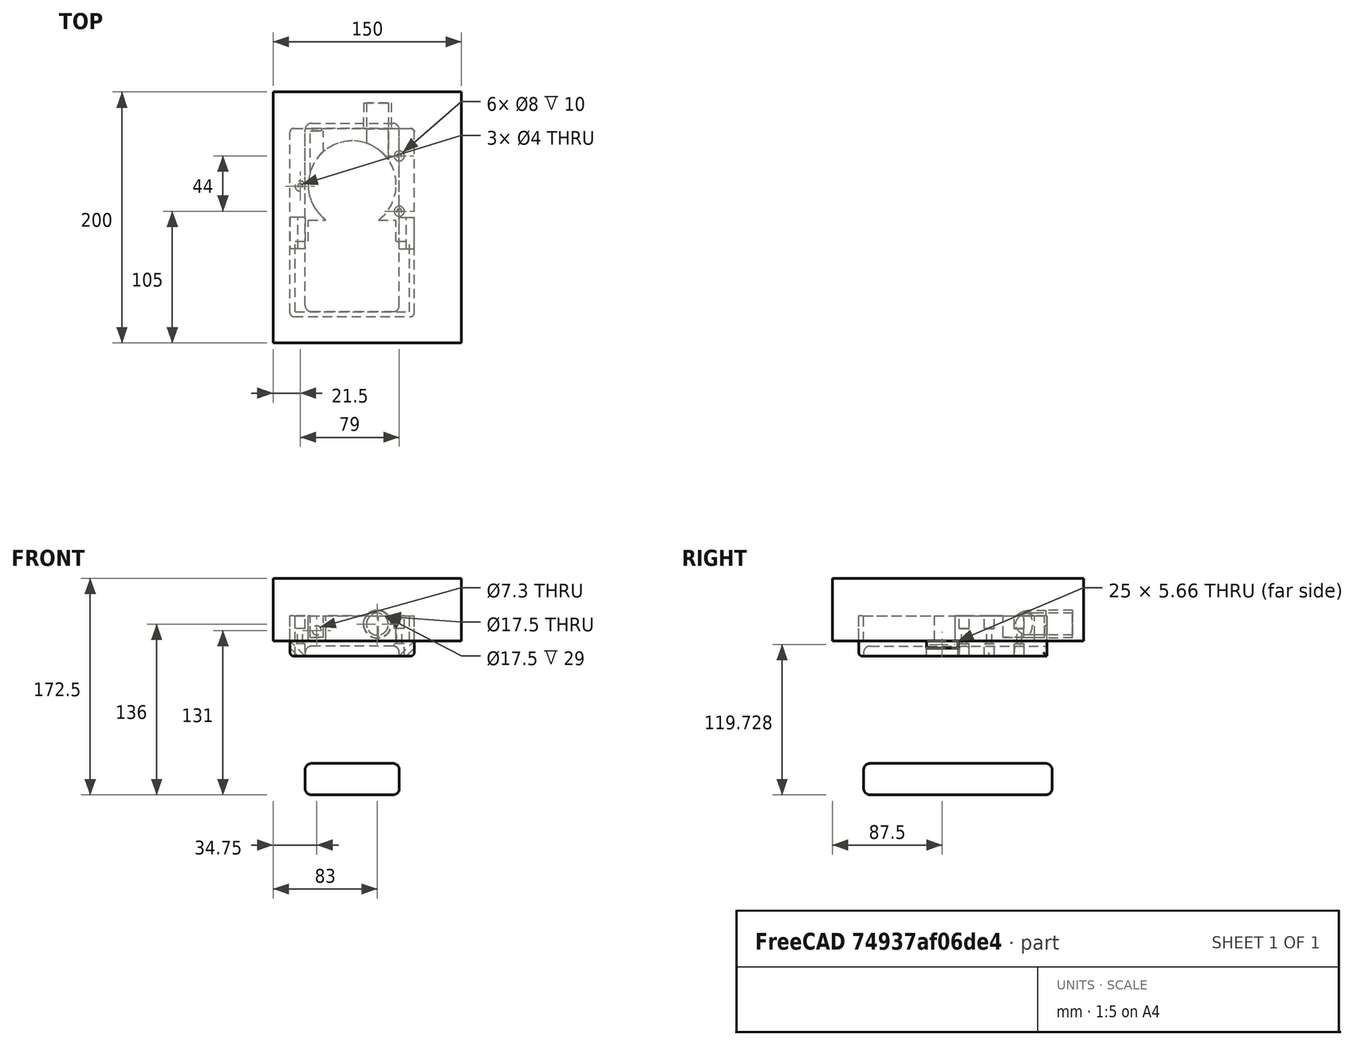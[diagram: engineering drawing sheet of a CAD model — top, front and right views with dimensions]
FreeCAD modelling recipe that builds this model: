
FCSTD DOCUMENT  (FreeCAD 0.18R4 (GitTag))
Label: PAPR-LOWER-image-view-V2
License: All rights reserved
LicenseURL: http://en.wikipedia.org/wiki/All_rights_reserved
objects: Part::Cylinder×17, Part::MultiFuse×11, Part::Box×8, Part::Fillet×7, Part::Cut×3, Part::Cone×2, Part::FeaturePython×1, Part::Mirroring×1
note: 50 computed .brp shape members not serialized (recipe doc carries the construction recipe); baked Part::Feature solids carry a one-line shape summary decoded from their .brp

FEATURE [Part::Cylinder] Cylinder  label="BlowerBody"
  Angle = 360
  AttacherType = Attacher::AttachEngine3D
  Height = 18
  Placement = pos=(0,0,4.5) rot=(0,0,1;0rad)
  Radius = 35
FEATURE [Part::Cylinder] Cylinder001  label="BlowerEndbearing"
  Angle = 360
  AttacherType = Attacher::AttachEngine3D
  Height = 5
  Placement = pos=(0,0,1) rot=(0,0,1;0rad)
  Radius = 2.25
FEATURE [Part::Cylinder] Cylinder002
  Angle = 360
  AttacherType = Attacher::AttachEngine3D
  Height = 10
  Placement = pos=(0,-28.4,0) rot=(0,0,1;0rad)
  Radius = 2
FEATURE [Part::FeaturePython] Array  label="BlowerFeet"  # Draft array (typed FeaturePython)
  Angle = 360
  ArrayType = 1
  Axis = (0,0,1)
  Base = -> Cylinder002
  Center = (0,0,0)
  Fuse = false
  IntervalAxis = (0,0,0)
  IntervalX = (1,0,0)
  IntervalY = (0,1,0)
  IntervalZ = (0,0,1)
  NumberPolar = 3
  NumberX = 1
  NumberY = 1
  NumberZ = 1
FEATURE [Part::Cylinder] Cylinder003  label="BlowerOutlet"
  Angle = 360
  AttacherType = Attacher::AttachEngine3D
  Height = 40
  Placement = pos=(20,36.3,13.5) rot=(1,0,0;1.5708rad)
  Radius = 8.75
FEATURE [Part::Cone] Cone  label="BlowerInlet"
  Angle = 360
  AttacherType = Attacher::AttachEngine3D
  Height = 13
  Placement = pos=(0,0,22.5) rot=(0,0,1;0rad)
  Radius1 = 27.25
  Radius2 = 27.15
FEATURE [Part::Cylinder] Cylinder004  label="BlowerBodyEnvelope"
  Angle = 360
  AttacherType = Attacher::AttachEngine3D
  Height = 25
  Radius = 35
FEATURE [Part::Cylinder] Cylinder005  label="OutletExtension"
  Angle = 360
  AttacherType = Attacher::AttachEngine3D
  Height = 40
  Placement = pos=(20,65.3,13.5) rot=(1,0,0;1.5708rad)
  Radius = 8.75
FEATURE [Part::Box] Box  label="DriverPocket"
  AttacherType = Attacher::AttachEngine3D
  Height = 20
  Length = 91
  Placement = pos=(-45.5,-106,0) rot=(0,0,1;0rad)
  Width = 56
FEATURE [Part::Box] Box001  label="WiringPocket"
  AttacherType = Attacher::AttachEngine3D
  Height = 20
  Length = 70
  Placement = pos=(-35,-53,0) rot=(0,0,1;0rad)
  Width = 20
FEATURE [Part::MultiFuse] Fusion  label="ElectronicsPocket"
  Placement = pos=(0,5,0) rot=(0,0,1;0rad)
  Shapes = -> [Box,Box001]
FEATURE [Part::Box] Box002  label="Potentiometer"
  AttacherType = Attacher::AttachEngine3D
  Height = 17
  Length = 10.5
  Placement = pos=(-30,18,5.5) rot=(0,0,1;0rad)
  Width = 35
FEATURE [Part::Cylinder] Cylinder006  label="Cylinder"
  Angle = 360
  AttacherType = Attacher::AttachEngine3D
  Height = 10
  Placement = pos=(-24.75,60.5,11) rot=(1,0,0;1.5708rad)
  Radius = 3.65
FEATURE [Part::MultiFuse] Fusion001  label="PotPocket"
  Placement = pos=(-3.5,-10,-2.5) rot=(0,0,1;0rad)
  Shapes = -> [Cylinder006,Box002]
FEATURE [Part::Box] Box004  label="HousingBlock"
  AttacherType = Attacher::AttachEngine3D
  Height = 32
  Length = 99
  Placement = pos=(-49.5,-105,-12) rot=(0,0,1;0rad)
  Width = 150
FEATURE [Part::Cylinder] Cylinder007  label="HousingOutlet"
  Angle = 360
  AttacherType = Attacher::AttachEngine3D
  Height = 40
  Placement = pos=(20,59.3,13.5) rot=(1,0,0;1.5708rad)
  Radius = 10.75
FEATURE [Part::MultiFuse] Fusion003  label="BlowerPocket"
  Shapes = -> [Cylinder004,Cone,Cylinder003,Array,Cylinder001,Cylinder]
FEATURE [Part::MultiFuse] Fusion004  label="CombinedPocket"
  Placement = pos=(0,0,104.5) rot=(0,0,1;0rad)
  Shapes = -> [Cylinder005,Fusion,Fusion001,Fusion003]
FEATURE [Part::Cone] Cone001  label="22mmTaper"
  Angle = 360
  AttacherType = Attacher::AttachEngine3D
  Height = 21
  Placement = pos=(20,65.3,13.5) rot=(0,-0.707107,0.707107;3.14159rad)
  Radius1 = 10.92
  Radius2 = 11.19
FEATURE [Part::MultiFuse] Fusion005  label="HousingLowerBody"
  Shapes = -> [Cone001,Cylinder007,Box004]
FEATURE [Part::Cut] Cut
  Base = -> Fusion005
  Tool = -> Fusion004
FEATURE [Part::Cylinder] Cylinder008  label="Cylinder003"
  Angle = 360
  AttacherType = Attacher::AttachEngine3D
  Height = 10
  Placement = pos=(-41.5,-1,10) rot=(0,0,1;0rad)
  Radius = 4
FEATURE [Part::Cylinder] Cylinder009  label="Cylinder004"
  Angle = 360
  AttacherType = Attacher::AttachEngine3D
  Height = 10
  Placement = pos=(37.5,-21,10) rot=(0,0,1;0rad)
  Radius = 4
FEATURE [Part::Cylinder] Cylinder010  label="Cylinder005"
  Angle = 360
  AttacherType = Attacher::AttachEngine3D
  Height = 10
  Placement = pos=(37.5,23,10) rot=(0,0,1;0rad)
  Radius = 4
FEATURE [Part::MultiFuse] Fusion006  label="TopMounting"
  Shapes = -> [Cylinder008,Cylinder009,Cylinder010]
FEATURE [Part::Cylinder] Cylinder011  label="Cylinder006"
  Angle = 360
  AttacherType = Attacher::AttachEngine3D
  Height = 30
  Placement = pos=(37.5,-21,10) rot=(0,0,1;0rad)
  Radius = 2
FEATURE [Part::Cylinder] Cylinder012  label="Cylinder007"
  Angle = 360
  AttacherType = Attacher::AttachEngine3D
  Height = 30
  Placement = pos=(37.5,23,10) rot=(0,0,1;0rad)
  Radius = 2
FEATURE [Part::Cylinder] Cylinder013  label="Cylinder008"
  Angle = 360
  AttacherType = Attacher::AttachEngine3D
  Height = 30
  Placement = pos=(-41.5,-1,10) rot=(0,0,1;0rad)
  Radius = 2
FEATURE [Part::MultiFuse] Fusion007  label="Mounting001"
  Placement = pos=(0,0,-30) rot=(0,0,1;0rad)
  Shapes = -> [Cylinder013,Cylinder011,Cylinder012]
FEATURE [Part::Cylinder] Cylinder014  label="Cylinder009"
  Angle = 360
  AttacherType = Attacher::AttachEngine3D
  Height = 20
  Placement = pos=(37.5,-21,10) rot=(0,0,1;0rad)
  Radius = 4
FEATURE [Part::Cylinder] Cylinder015  label="Cylinder010"
  Angle = 360
  AttacherType = Attacher::AttachEngine3D
  Height = 20
  Placement = pos=(37.5,23,10) rot=(0,0,1;0rad)
  Radius = 4
FEATURE [Part::Cylinder] Cylinder016  label="Cylinder011"
  Angle = 360
  AttacherType = Attacher::AttachEngine3D
  Height = 20
  Placement = pos=(-41.5,-1,10) rot=(0,0,1;0rad)
  Radius = 4
FEATURE [Part::MultiFuse] Fusion008  label="Mounting002"
  Placement = pos=(0,0,-32) rot=(0,0,1;0rad)
  Shapes = -> [Cylinder016,Cylinder014,Cylinder015]
FEATURE [Part::MultiFuse] Fusion009  label="BottomMounting"
  Shapes = -> [Fusion007,Fusion008]
FEATURE [Part::MultiFuse] Fusion010  label="CombinedMounting"
  Shapes = -> [Fusion006,Fusion009]
FEATURE [Part::Cut] Cut001
  Base = -> Cut
  Tool = -> Fusion010
FEATURE [Part::Box] Box005  label="Slot1"
  AttacherType = Attacher::AttachEngine3D
  Height = 4
  Length = 25
  Placement = pos=(-37.4228,-51,-17.6777) rot=(0.357407,0.357407,0.862856;1.71777rad)
  Width = 40
FEATURE [Part::Box] Box006  label="Slot2"
  AttacherType = Attacher::AttachEngine3D
  Height = 4
  Length = 25
  Placement = pos=(-37.4228,-44,-17.6777) rot=(0.357407,0.357407,0.862856;1.71777rad)
  Width = 40
FEATURE [Part::Mirroring] Part__Mirroring  label="Slot2 (Mirror #1)"
  Base = (0,0,0)
  Normal = (1,0,0)
  Placement = pos=(0,-7,0) rot=(0,0,1;0rad)
  Source = -> Box006
FEATURE [Part::MultiFuse] Fusion011  label="StrapSlots"
  Shapes = -> [Box005,Part__Mirroring]
FEATURE [Part::Cut] Cut002  label="PAPR-Lower-Housing"
  Base = -> Cut001
  Tool = -> Fusion011
FEATURE [Part::Box] Box007  label="Cube001"
  AttacherType = Attacher::AttachEngine3D
  Height = 50
  Length = 150
  Placement = pos=(-63,-126,0) rot=(0,0,1;0rad)
  Width = 200
FEATURE [Part::Fillet] Fillet006
  Base = -> Cut002
  Edges = 7 edges r=3: [Edge37,Edge45,Edge51,Edge52,Edge57,Edge58,Edge59]
FEATURE [Part::Box] Box003  label="Cube"
  AttacherType = Attacher::AttachEngine3D
  Height = 25
  Length = 75
  Placement = pos=(-37.5,-101,-29) rot=(0,0,1;0rad)
  Width = 150
FEATURE [Part::Fillet] Fillet
  Base = -> Box003
  Edges = 1 edges r=5: [Edge2]
FEATURE [Part::Fillet] Fillet001
  Base = -> Fillet
  Edges = 1 edges r=5: [Edge3]
FEATURE [Part::Fillet] Fillet002
  Base = -> Fillet001
  Edges = 1 edges r=5: [Edge17]
FEATURE [Part::Fillet] Fillet003
  Base = -> Fillet002
  Edges = 1 edges r=5: [Edge15]
FEATURE [Part::Fillet] Fillet004
  Base = -> Fillet003
  Edges = 1 edges r=5: [Edge18]
FEATURE [Part::Fillet] Fillet005  label="BatteryPocket"
  Base = -> Fillet004
  Edges = 4 edges r=5: [Edge3,Edge12,Edge13,Edge16]
  Placement = pos=(0,0,-93.5) rot=(0,0,1;0rad)
